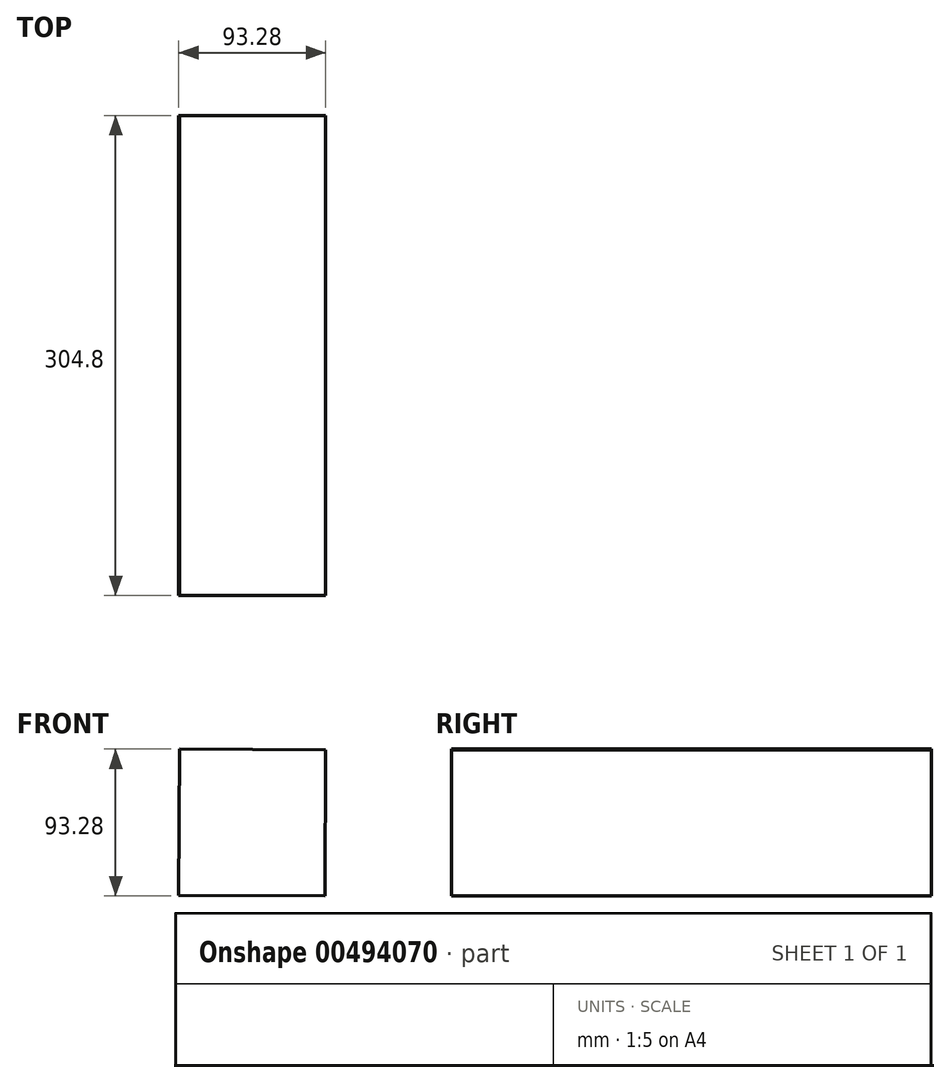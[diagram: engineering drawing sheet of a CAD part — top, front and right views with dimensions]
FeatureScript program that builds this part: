
annotation { "Feature Type Name" : "Feature", "Feature Type Description" : "" }
export const myFeature = defineFeature(function(context is Context, id is Id, definition is map)
    precondition{}
    {
        {
            var Q0;
            Q0=qCreatedBy(makeId("Front.planeOp"),FACE);
            var sketch = newSketch(context, id + "F0", { "sketchPlane" : qUnion([Q0])});
            skCircle(sketch, "E0.cCircle", {"center": v(0, 0) * mm, "radius": 65.64 * mm, "construction": true});
            skLineSegment(sketch, "E0.0", {"start": v(-46.2, 46.64) * mm, "end": v(46.64, 46.2) * mm});
            skLineSegment(sketch, "E0.1", {"start": v(46.64, 46.2) * mm, "end": v(46.2, -46.64) * mm});
            skLineSegment(sketch, "E0.2", {"start": v(46.2, -46.64) * mm, "end": v(-46.64, -46.2) * mm});
            skLineSegment(sketch, "E0.3", {"start": v(-46.64, -46.2) * mm, "end": v(-46.2, 46.64) * mm});
            skSolve(sketch);
        }
        {
            var Q0;
            Q0=makeQuery(id+"F0.imprint","IMPRINT",FACE,{"disambiguationData":[TD([[makeQuery(id+"F0.imprint","IMPRINT",EDGE,{"derivedFrom":sQuery(id+"F0.wireOp",EDGE,"E0.0")}),-1.0]])]});
            extrude(context, id + "F1", {"entities" : qUnion([Q0]), "depth" : 304.8 * mm});
        }
    });
